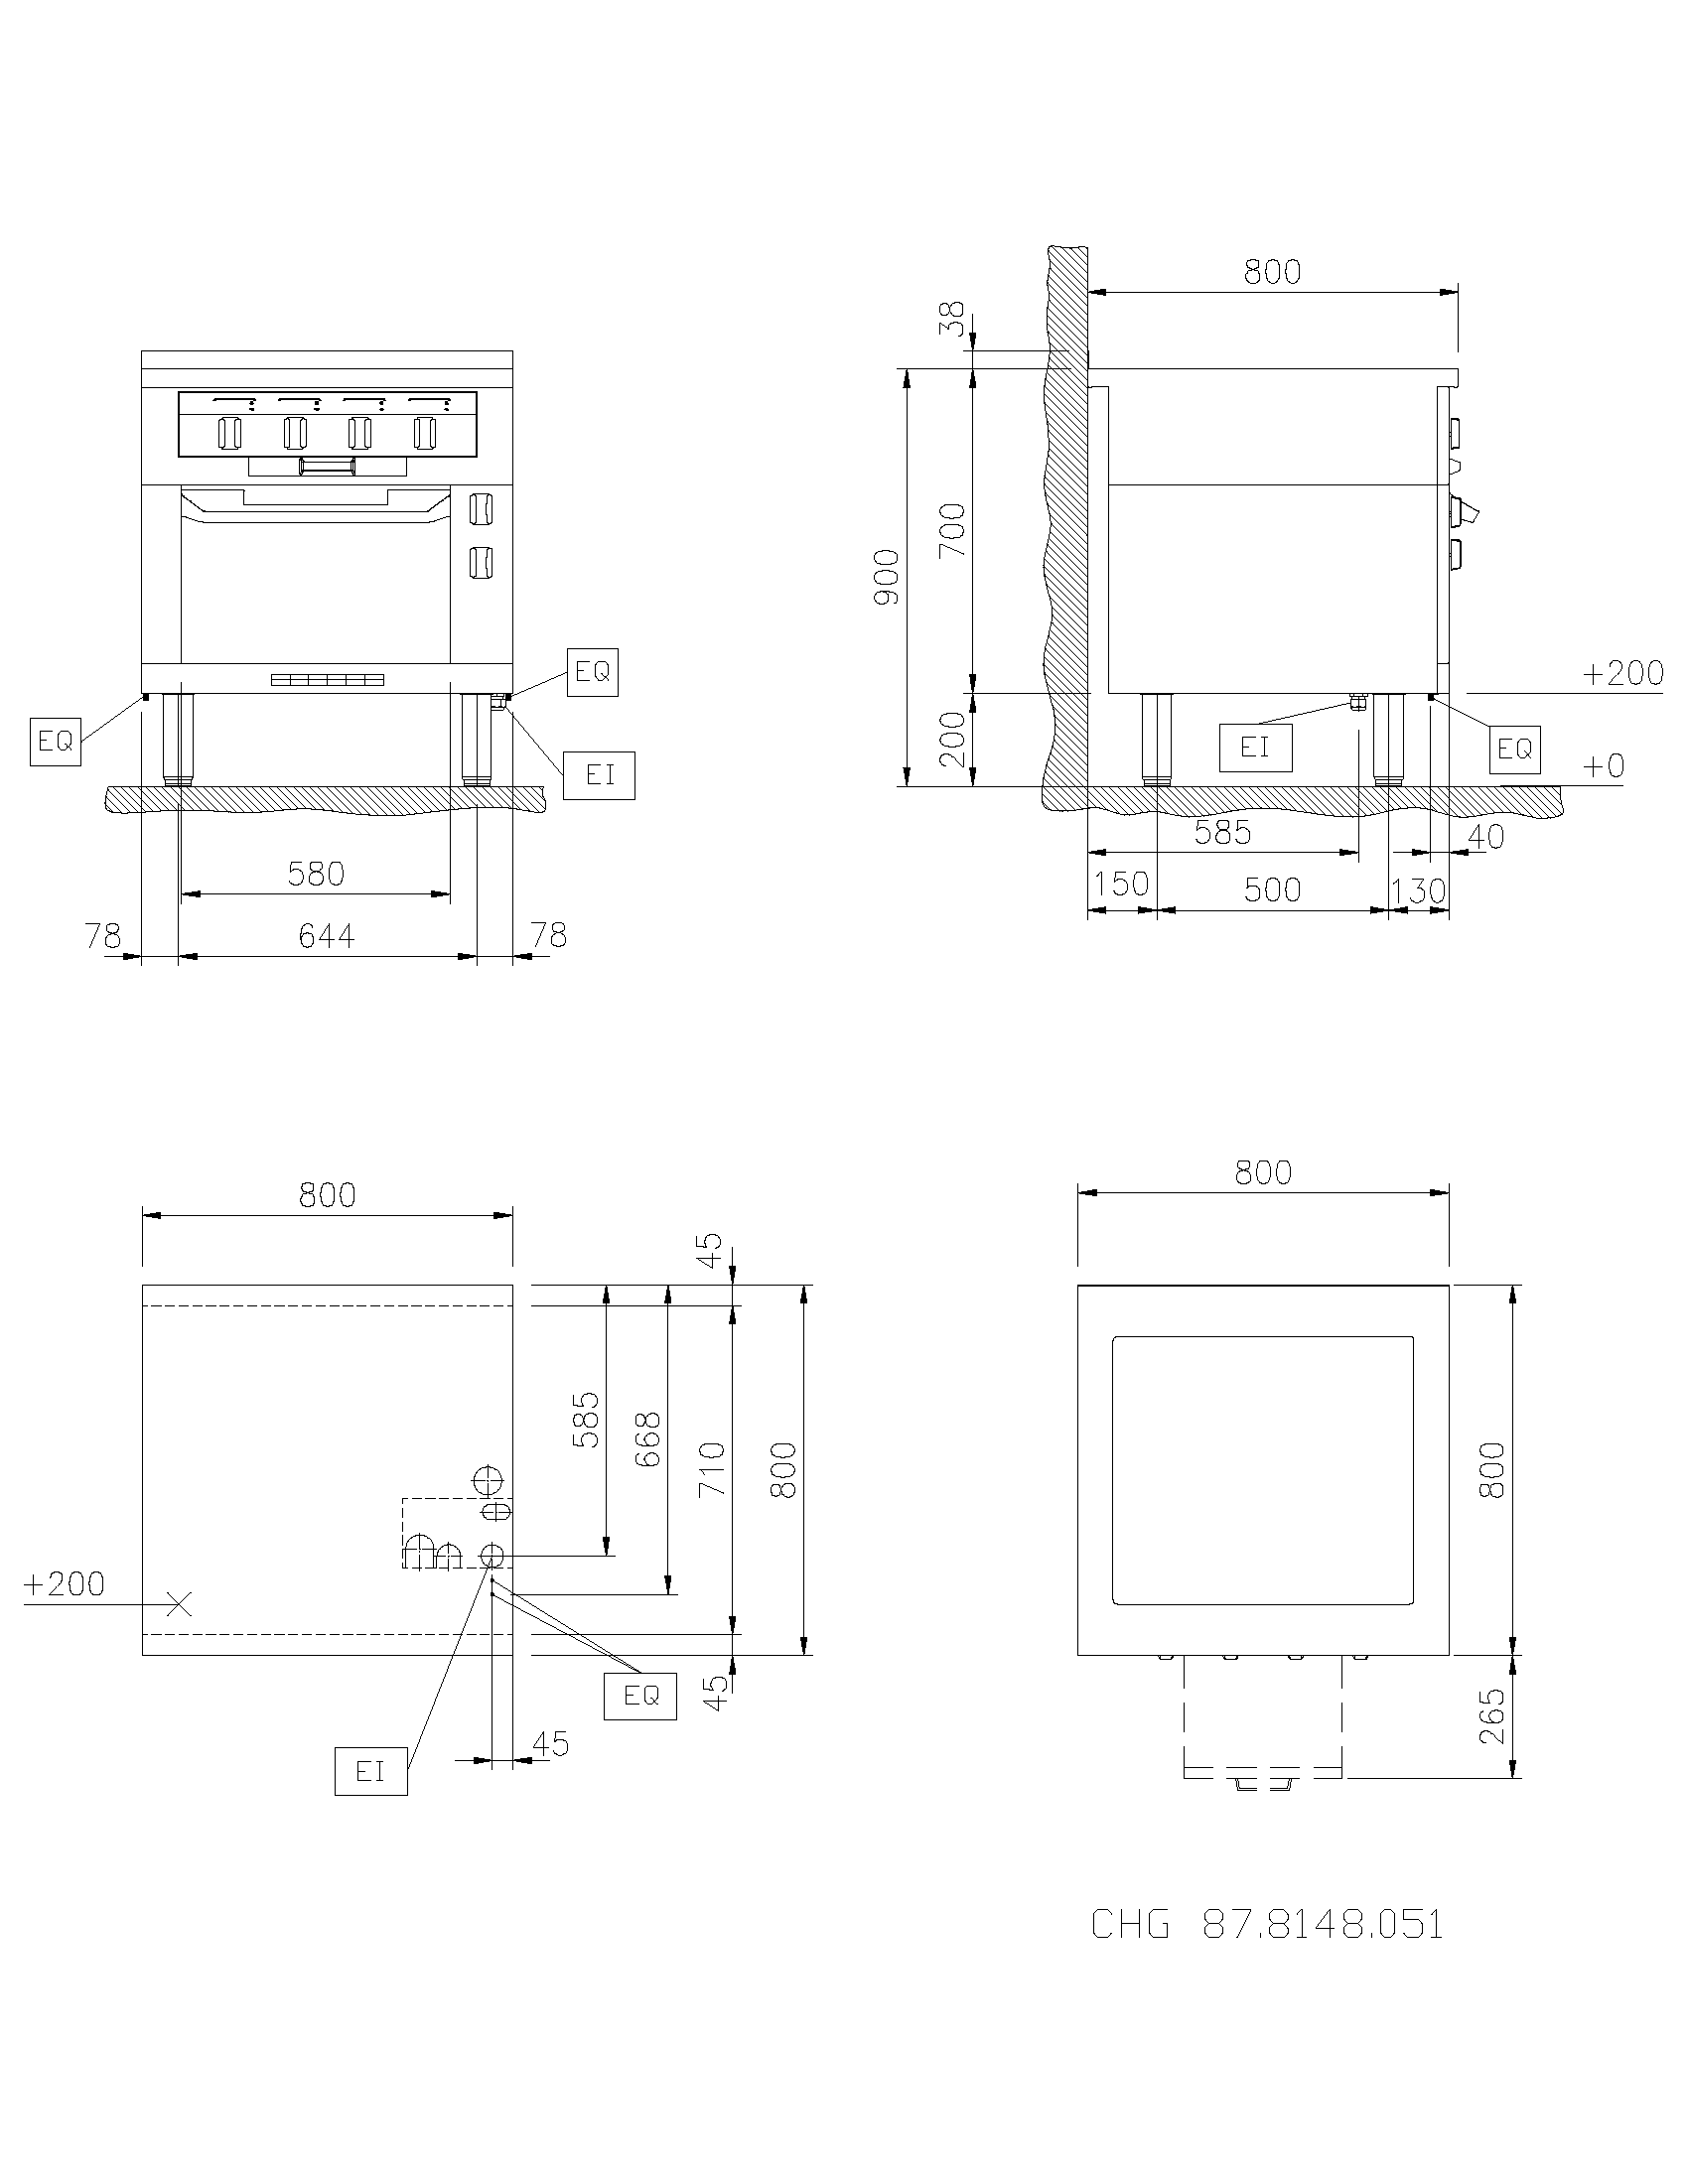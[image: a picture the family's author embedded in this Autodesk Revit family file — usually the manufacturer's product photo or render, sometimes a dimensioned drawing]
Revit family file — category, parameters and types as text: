
# Revit family: QF_ELECTROLUXPROFESSIONAL_588465_MALRFCH4AO
name_source: partatom
category: Attrezzature speciali
units: mm (PartAtom-declared; Revit-internal decimal feet)

## family parameters
Basato su piano di lavoro = No
Condiviso = No
Punto di calcolo locali = No
Quota connettore circolare = Usa diametro
Sempre verticale = Sì
Taglio con vuoti quando caricato = No
Tipo di parte = Normale

## types (1)
- Standard
    Accessory = Sì
    Cold Water Size = 0"
    Compressed Air Pressure = 0.00 psi
    Compressed Air Size = 0"
    Compressed Air Volume = 0 GPM
    Condensate Return Size = 0"
    Cycle = 50 Hz
    Depth Actual = 800 mm  [stored 2.62467 ft]
    Descrizione = EL.SOLID TOP,WARM.CAB.PASS,2S,800X800X8
    Direct Waste Size = 0"
    Gas Input Pressure = 0.0
    Gas KW = 0
    Gas Size = 0"
    HP = 19.2 HP
    Height Actual = 800 mm  [stored 2.62467 ft]
    Hot Water Size = 0"
    Item Number = 588465
    Length Actual = 800 mm  [stored 2.62467 ft]
    Modello = MALRFCH4AO
    Phase = 3
    Produttore = Electrolux Professional
    Prospetto di default = 0 mm  [stored 0 ft]
    Refrigerant Compressor Remote = Sì
    Refrigeration Liquid Line Size = 0 mm  [stored 0 ft]
    Refrigeration Suction Line Size = 0 mm  [stored 0 ft]
    Steam Consumption per Hour = 0
    Steam Supply Maximum Pressure = 0.00 psi
    Steam Supply Minimum Pressure = 0.00 psi
    Steam Supply Size = 0"
    URL = https://www.electroluxprofessional.com
    URL Manufacturer = https://www.electroluxprofessional.com
    Volts = 400 V
    Watts = 14300 W
    Weight = 147.00 kg

note: source unit labels omitted for Gas Input Pressure — the stored unit's dimension contradicts the parameter name (converter mislabeling)

note: [stored X ft] marks values corroborated as IEEE doubles in the binary element streams (Revit-internal decimal feet)

## geometry (parser evidence)
native form markers: Blend x12, Sweep x13
no freeform markers — native parametric forms only
